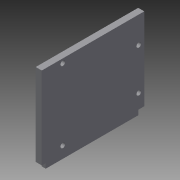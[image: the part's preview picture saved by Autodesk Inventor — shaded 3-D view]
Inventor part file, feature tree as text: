
AUTODESK INVENTOR PART (.ipt)
format: ipt  version: 2015 SP2 (Build 190223200, 223)  size: 101,888 bytes
history: native  units: in
note: dims shown in document units (in); Inventor stores cm internally (conversion verified against a paired STEP export)
features: sketch x3, extrude x2, plane x1, hole x1
ambient origin geometry x8: Origin, YZ Plane, XZ Plane, XY Plane, X Axis, Y Axis, Z Axis, Center Point
bodies: Solid1 (feature_tree)
feature tree (7):
  plane  "Work Plane1"
  extrude  "Extrusion1"  Depth=0.1063in
  extrude  "Extrusion2"  Depth=0.1575in TaperAngle=0.0deg
  hole  "Hole2"  [1 undecoded]
  sketch  "Sketch1"  dims[d0=2.2047in d1=0.0in d14=0.1063in]
  sketch  "Sketch3"  dims[d15=2.4803in d16=0.1575in d17=0.0in]
  sketch  "Sketch4"  dims[d20=0.126in d22=0.126in d24=0.1092in d25=0.126in d27=0.126in d28=0.126in d29=0.2362in d30=0.1575in d31=0.0787in d32=90.0deg d33=0.315in d34=0.8108in]
note: 1 required parameter value undecoded (feature->parameter linkage not recoverable at this tier; creation-order binding heuristic only, values carry confidence <= 0.55)
